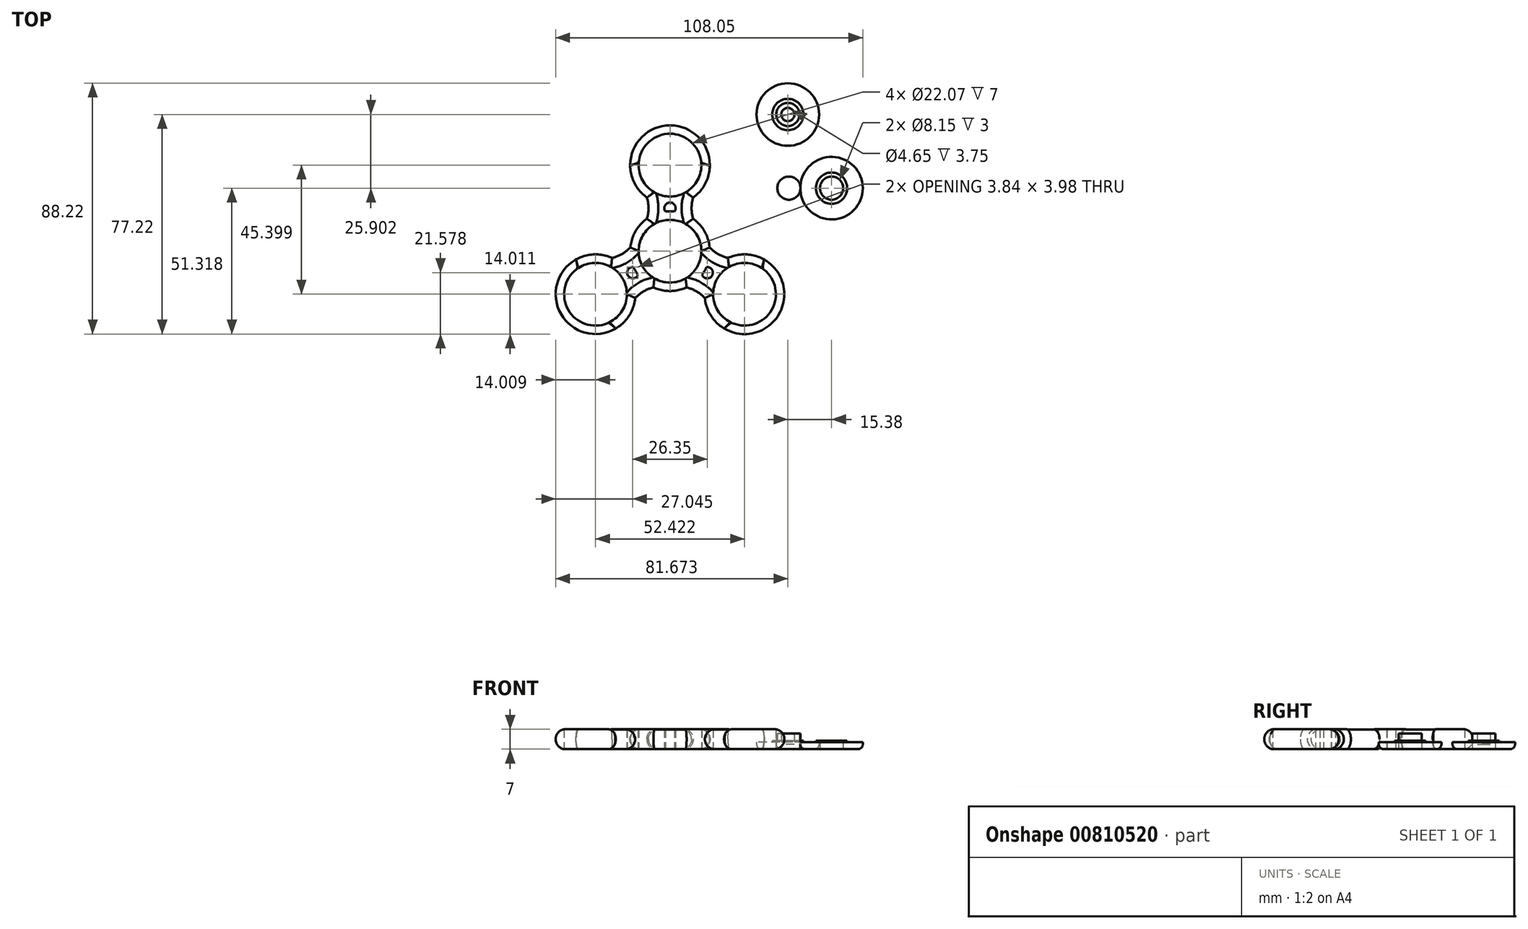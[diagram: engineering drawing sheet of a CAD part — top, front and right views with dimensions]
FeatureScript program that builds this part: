
annotation { "Feature Type Name" : "Feature", "Feature Type Description" : "" }
export const myFeature = defineFeature(function(context is Context, id is Id, definition is map)
    precondition{}
    {
        {
            var Q0;
            Q0=qCreatedBy(makeId("Top.planeOp"),FACE);
            var sketch = newSketch(context, id + "F0", { "sketchPlane" : qUnion([Q0])});
            skLineSegment(sketch, "E0.0", {"start": v(14.14, 16.04) * mm, "end": v(14.14, -14.2) * mm});
            skLineSegment(sketch, "E0.1", {"start": v(14.14, -14.2) * mm, "end": v(-14.14, -14.2) * mm});
            skLineSegment(sketch, "E0.2", {"start": v(-14.14, -14.2) * mm, "end": v(-14.14, 16.08) * mm});
            skLineSegment(sketch, "E0.3", {"start": v(-14.14, 16.08) * mm, "end": v(14.14, 16.04) * mm});
            skPoint(sketch, "E0.0.midPoint", {"position": v(14.14, 0.92) * mm});
            skCircle(sketch, "E1", {"center": v(0, 16.06) * mm, "radius": 14.01 * mm});
            skCircle(sketch, "E2", {"center": v(0, 16.06) * mm, "radius": 11.04 * mm});
            skCircle(sketch, "E3", {"center": v(0, -14.2) * mm, "radius": 14.01 * mm});
            skCircle(sketch, "E4", {"center": v(0, -14.2) * mm, "radius": 11.04 * mm});
            skPoint(sketch, "E5", {"position": v(7.58, 0.92) * mm});
            skPoint(sketch, "E6", {"position": v(-7.58, 0.92) * mm});
            skPoint(sketch, "E7", {"position": v(-14.14, 0.92) * mm});
            skFitSpline(sketch, "E8", {"points": [v(-14.14, 16.08) * mm, v(-7.58, 0.92) * mm, v(-14.14, -14.2) * mm], "startDerivative": vector(19.66, -30.33) * mm, "endDerivative": vector(-19.67, -30.25) * mm});
            skFitSpline(sketch, "E9", {"points": [v(14.14, 16.04) * mm, v(7.58, 0.92) * mm, v(14.14, -14.2) * mm], "startDerivative": vector(-19.67, -30.24) * mm, "endDerivative": vector(19.67, -30.24) * mm});
            skCircle(sketch, "E10", {"center": v(0, 0.92) * mm, "radius": 2 * mm});
            skPoint(sketch, "E11", {"position": v(0, 30.07) * mm});
            skPoint(sketch, "E12", {"position": v(10.48, 25.36) * mm});
            skPoint(sketch, "E13", {"position": v(-10.48, 25.36) * mm});
            skSolve(sketch);
        }
        {
            var Q0;
            Q0=qCreatedBy(makeId("Top.planeOp"),FACE);
            var sketch = newSketch(context, id + "F1", { "sketchPlane" : qUnion([Q0])});
            skCircle(sketch, "E14", {"center": v(41.45, 33.87) * mm, "radius": 11 * mm});
            skCircle(sketch, "E15", {"center": v(41.45, 33.87) * mm, "radius": 5.5 * mm});
            skCircle(sketch, "E16", {"center": v(41.45, 33.87) * mm, "radius": 4.08 * mm});
            skCircle(sketch, "E17", {"center": v(41.83, 7.97) * mm, "radius": 11 * mm});
            skCircle(sketch, "E18", {"center": v(41.83, 7.97) * mm, "radius": 5.5 * mm});
            skCircle(sketch, "E19", {"center": v(41.83, 7.97) * mm, "radius": 4.08 * mm});
            skSolve(sketch);
        }
        {
            var Q0;
            {var subQ1=sQuery(id+"F0.wireOp",EDGE,"E1");var subQ6=sQuery(id+"F0.wireOp",EDGE,"E0.3");var subQ13=makeQuery(id+"F0.imprint","INTERSECT",VERTEX,{"disambiguationData":[OD(0.0)],"derivedFrom":[subQ6,subQ1]});Q0=makeQuery(id+"F0.imprint","IMPRINT",FACE,{"disambiguationData":[TD([[makeQuery(id+"F0.imprint","IMPRINT",EDGE,{"disambiguationData":[TD([[subQ13,-1.0]])],"derivedFrom":subQ6}),1.0]])]});}
            var Q1;
            {var subQ0=sQuery(id+"F0.wireOp",EDGE,"pasm8Eyo-fXrZ-fvG0-8Elu-paJzOGyL3H0m");Q1=makeQuery(id+"F0.imprint","IMPRINT",FACE,{"disambiguationData":[TD([[makeQuery(id+"F0.imprint","IMPRINT",EDGE,{"derivedFrom":subQ0}),1.0]])]});}
            var Q2;
            {var subQ0=sQuery(id+"F0.wireOp",EDGE,"ogIBovJo-0tES-EHRu-C9qO-bWghCShUOrSJ");Q2=makeQuery(id+"F0.imprint","IMPRINT",FACE,{"disambiguationData":[TD([[makeQuery(id+"F0.imprint","IMPRINT",EDGE,{"derivedFrom":subQ0}),1.0]])]});}
            var Q3;
            {var subQ0=sQuery(id+"F0.wireOp",EDGE,"de5ad749-d6f0-4c98-9bd6-3e4d16faad500.MirrorCS");var subQ1=sQuery(id+"F0.wireOp",EDGE,"E1");var subQ2=makeQuery(id+"F0.imprint","INTERSECT",VERTEX,{"disambiguationData":[OD(0.0)],"derivedFrom":[subQ1,subQ0]});Q3=makeQuery(id+"F0.imprint","IMPRINT",FACE,{"disambiguationData":[TD([[makeQuery(id+"F0.imprint","IMPRINT",EDGE,{"disambiguationData":[TD([[subQ2,1.0]])],"derivedFrom":subQ1}),-1.0]])]});}
            var Q4;
            {var subQ0=sQuery(id+"F0.wireOp",EDGE,"005f5cdd-0bdc-4fa0-b84f-56ab7e4a56270.MirrorCS");var subQ3=sQuery(id+"F0.wireOp",EDGE,"E1");var subQ5=makeQuery(id+"F0.imprint","INTERSECT",VERTEX,{"derivedFrom":[subQ3,subQ0]});Q4=makeQuery(id+"F0.imprint","IMPRINT",FACE,{"disambiguationData":[TD([[makeQuery(id+"F0.imprint","IMPRINT",EDGE,{"disambiguationData":[TD([[subQ5,1.0]])],"derivedFrom":subQ3}),-1.0]])]});}
            var Q5;
            {var subQ0=sQuery(id+"F0.wireOp",EDGE,"E9");var subQ1=sQuery(id+"F0.wireOp",EDGE,"E1");var subQ2=makeQuery(id+"F0.imprint","INTERSECT",VERTEX,{"disambiguationData":[OD(0.0)],"derivedFrom":[subQ1,subQ0]});Q5=makeQuery(id+"F0.imprint","IMPRINT",FACE,{"disambiguationData":[TD([[makeQuery(id+"F0.imprint","IMPRINT",EDGE,{"disambiguationData":[TD([[subQ2,-1.0]])],"derivedFrom":subQ1}),1.0]])]});}
            var Q6;
            {var subQ1=sQuery(id+"F0.wireOp",EDGE,"E1");var subQ5=sQuery(id+"F0.wireOp",EDGE,"E0.3");var subQ6=makeQuery(id+"F0.imprint","INTERSECT",VERTEX,{"disambiguationData":[OD(0.0)],"derivedFrom":[subQ5,subQ1]});Q6=makeQuery(id+"F0.imprint","IMPRINT",FACE,{"disambiguationData":[TD([[makeQuery(id+"F0.imprint","IMPRINT",EDGE,{"disambiguationData":[TD([[subQ6,-1.0]])],"derivedFrom":subQ5}),-1.0]])]});}
            var Q7;
            {var subQ0=sQuery(id+"F0.wireOp",EDGE,"E8");var subQ1=sQuery(id+"F0.wireOp",EDGE,"E1");var subQ2=makeQuery(id+"F0.imprint","INTERSECT",VERTEX,{"disambiguationData":[OD(0.0)],"derivedFrom":[subQ1,subQ0]});Q7=makeQuery(id+"F0.imprint","IMPRINT",FACE,{"disambiguationData":[TD([[makeQuery(id+"F0.imprint","IMPRINT",EDGE,{"disambiguationData":[TD([[subQ2,-1.0]])],"derivedFrom":subQ1}),1.0]])]});}
            var Q8;
            {var subQ0=sQuery(id+"F0.wireOp",EDGE,"E8");var subQ1=sQuery(id+"F0.wireOp",EDGE,"E1");var subQ2=makeQuery(id+"F0.imprint","INTERSECT",VERTEX,{"disambiguationData":[OD(1.0)],"derivedFrom":[subQ1,subQ0]});Q8=makeQuery(id+"F0.imprint","IMPRINT",FACE,{"disambiguationData":[TD([[makeQuery(id+"F0.imprint","IMPRINT",EDGE,{"disambiguationData":[TD([[subQ2,-1.0]])],"derivedFrom":subQ1}),-1.0]])]});}
            var Q9;
            {var subQ0=sQuery(id+"F0.wireOp",EDGE,"E10");var subQ1=sQuery(id+"F0.wireOp",EDGE,"E1");var subQ2=makeQuery(id+"F0.imprint","INTERSECT",VERTEX,{"disambiguationData":[OD(1.0)],"derivedFrom":[subQ1,subQ0]});Q9=makeQuery(id+"F0.imprint","IMPRINT",FACE,{"disambiguationData":[TD([[makeQuery(id+"F0.imprint","IMPRINT",EDGE,{"disambiguationData":[TD([[subQ2,-1.0]])],"derivedFrom":subQ1}),-1.0]])]});}
            var Q10;
            {var subQ0=sQuery(id+"F0.wireOp",EDGE,"E8");var subQ1=sQuery(id+"F0.wireOp",EDGE,"E3");var subQ2=makeQuery(id+"F0.imprint","INTERSECT",VERTEX,{"disambiguationData":[OD(0.0)],"derivedFrom":[subQ1,subQ0]});Q10=makeQuery(id+"F0.imprint","IMPRINT",FACE,{"disambiguationData":[TD([[makeQuery(id+"F0.imprint","IMPRINT",EDGE,{"disambiguationData":[TD([[subQ2,-1.0]])],"derivedFrom":subQ1}),1.0]])]});}
            var Q11;
            {var subQ0=sQuery(id+"F0.wireOp",EDGE,"E9");var subQ1=sQuery(id+"F0.wireOp",EDGE,"E3");var subQ2=makeQuery(id+"F0.imprint","INTERSECT",VERTEX,{"disambiguationData":[OD(0.0)],"derivedFrom":[subQ1,subQ0]});Q11=makeQuery(id+"F0.imprint","IMPRINT",FACE,{"disambiguationData":[TD([[makeQuery(id+"F0.imprint","IMPRINT",EDGE,{"disambiguationData":[TD([[subQ2,-1.0]])],"derivedFrom":subQ1}),1.0]])]});}
            var Q12;
            {var subQ0=sQuery(id+"F0.wireOp",EDGE,"E3");var subQ1=sQuery(id+"F0.wireOp",EDGE,"E0.1");var subQ2=makeQuery(id+"F0.imprint","INTERSECT",VERTEX,{"disambiguationData":[OD(0.0)],"derivedFrom":[subQ1,subQ0]});Q12=makeQuery(id+"F0.imprint","IMPRINT",FACE,{"disambiguationData":[TD([[makeQuery(id+"F0.imprint","IMPRINT",EDGE,{"disambiguationData":[TD([[subQ2,-1.0]])],"derivedFrom":subQ1}),1.0]])]});}
            var Q13;
            {var subQ1=sQuery(id+"F0.wireOp",EDGE,"E3");var subQ5=sQuery(id+"F0.wireOp",EDGE,"E0.1");var subQ6=makeQuery(id+"F0.imprint","INTERSECT",VERTEX,{"disambiguationData":[OD(0.0)],"derivedFrom":[subQ5,subQ1]});Q13=makeQuery(id+"F0.imprint","IMPRINT",FACE,{"disambiguationData":[TD([[makeQuery(id+"F0.imprint","IMPRINT",EDGE,{"disambiguationData":[TD([[subQ6,-1.0]])],"derivedFrom":subQ5}),-1.0]])]});}
            extrude(context, id + "F2", {"entities" : qUnion([Q0, Q1, Q2, Q3, Q4, Q5, Q6, Q7, Q8, Q9, Q10, Q11, Q12, Q13]), "depth" : 7 * mm, "offsetDistance" : 25 * mm});
        }
        {
            var Q0;
            Q0=makeQuery(id+"F2.opExtrude","SWEPT_BODY",BODY,{"disambiguationData":[OSD([sQuery(id+"F0.wireOp",EDGE,"E0.0"),sQuery(id+"F0.wireOp",EDGE,"E0.1"),sQuery(id+"F0.wireOp",EDGE,"E0.2"),sQuery(id+"F0.wireOp",EDGE,"E0.3"),sQuery(id+"F0.wireOp",EDGE,"E1"),sQuery(id+"F0.wireOp",EDGE,"E2"),sQuery(id+"F0.wireOp",EDGE,"E3"),sQuery(id+"F0.wireOp",EDGE,"E4")])]});
            var Q1;
            Q1=sQuery(id+"F0.wireOp",EDGE,"E4");
            circularPattern(context, id + "F3", {"entities" : qUnion([Q0]), "axis" : qUnion([Q1]), "angle" : 360 * degree, "instanceCount" : 3, "equalSpace" : true});
        }
        {
            var Q0;
            Q0=makeQuery(id+"F2.opExtrude","SWEPT_BODY",BODY,{"disambiguationData":[OSD([sQuery(id+"F0.wireOp",EDGE,"E0.0"),sQuery(id+"F0.wireOp",EDGE,"E0.1"),sQuery(id+"F0.wireOp",EDGE,"E0.2"),sQuery(id+"F0.wireOp",EDGE,"E0.3"),sQuery(id+"F0.wireOp",EDGE,"E1"),sQuery(id+"F0.wireOp",EDGE,"E2"),sQuery(id+"F0.wireOp",EDGE,"E3"),sQuery(id+"F0.wireOp",EDGE,"E4")])]});
            var Q1;
            Q1=makeQuery(id+"F3.opPattern","COPY",BODY,{"derivedFrom":makeQuery(id+"F2.opExtrude","SWEPT_BODY",BODY,{"disambiguationData":[OSD([sQuery(id+"F0.wireOp",EDGE,"E0.0"),sQuery(id+"F0.wireOp",EDGE,"E0.1"),sQuery(id+"F0.wireOp",EDGE,"E0.2"),sQuery(id+"F0.wireOp",EDGE,"E0.3"),sQuery(id+"F0.wireOp",EDGE,"E1"),sQuery(id+"F0.wireOp",EDGE,"E2"),sQuery(id+"F0.wireOp",EDGE,"E3"),sQuery(id+"F0.wireOp",EDGE,"E4")])]}),"instanceName":"3"});
            var Q2;
            Q2=makeQuery(id+"F3.opPattern","COPY",BODY,{"derivedFrom":makeQuery(id+"F2.opExtrude","SWEPT_BODY",BODY,{"disambiguationData":[OSD([sQuery(id+"F0.wireOp",EDGE,"E0.0"),sQuery(id+"F0.wireOp",EDGE,"E0.1"),sQuery(id+"F0.wireOp",EDGE,"E0.2"),sQuery(id+"F0.wireOp",EDGE,"E0.3"),sQuery(id+"F0.wireOp",EDGE,"E1"),sQuery(id+"F0.wireOp",EDGE,"E2"),sQuery(id+"F0.wireOp",EDGE,"E3"),sQuery(id+"F0.wireOp",EDGE,"E4")])]}),"instanceName":"4"});
            var Q3;
            Q3=makeQuery(id+"F3.opPattern","COPY",BODY,{"derivedFrom":makeQuery(id+"F2.opExtrude","SWEPT_BODY",BODY,{"disambiguationData":[OSD([sQuery(id+"F0.wireOp",EDGE,"E0.0"),sQuery(id+"F0.wireOp",EDGE,"E0.1"),sQuery(id+"F0.wireOp",EDGE,"E0.2"),sQuery(id+"F0.wireOp",EDGE,"E0.3"),sQuery(id+"F0.wireOp",EDGE,"E1"),sQuery(id+"F0.wireOp",EDGE,"E2"),sQuery(id+"F0.wireOp",EDGE,"E3"),sQuery(id+"F0.wireOp",EDGE,"E4")])]}),"instanceName":"1"});
            var Q4;
            Q4=makeQuery(id+"F3.opPattern","COPY",BODY,{"derivedFrom":makeQuery(id+"F2.opExtrude","SWEPT_BODY",BODY,{"disambiguationData":[OSD([sQuery(id+"F0.wireOp",EDGE,"E0.0"),sQuery(id+"F0.wireOp",EDGE,"E0.1"),sQuery(id+"F0.wireOp",EDGE,"E0.2"),sQuery(id+"F0.wireOp",EDGE,"E0.3"),sQuery(id+"F0.wireOp",EDGE,"E1"),sQuery(id+"F0.wireOp",EDGE,"E2"),sQuery(id+"F0.wireOp",EDGE,"E3"),sQuery(id+"F0.wireOp",EDGE,"E4")])]}),"instanceName":"2"});
            var Q5;
            Q5=makeQuery(id+"F3.opPattern","COPY",BODY,{"derivedFrom":makeQuery(id+"F2.opExtrude","SWEPT_BODY",BODY,{"disambiguationData":[OSD([sQuery(id+"F0.wireOp",EDGE,"E0.0"),sQuery(id+"F0.wireOp",EDGE,"E0.1"),sQuery(id+"F0.wireOp",EDGE,"E0.2"),sQuery(id+"F0.wireOp",EDGE,"E0.3"),sQuery(id+"F0.wireOp",EDGE,"E1"),sQuery(id+"F0.wireOp",EDGE,"E2"),sQuery(id+"F0.wireOp",EDGE,"E3"),sQuery(id+"F0.wireOp",EDGE,"E4")])]}),"instanceName":"5"});
            booleanBodies(context, id + "F4", {"operationType" : BooleanOperationType.UNION, "tools" : qUnion([Q0, Q1, Q2, Q3, Q4, Q5])});
        }
        {
            var Q0;
            Q0=makeQuery(id+"F1.imprint","IMPRINT",FACE,{"disambiguationData":[TD([[makeQuery(id+"F1.imprint","IMPRINT",EDGE,{"derivedFrom":sQuery(id+"F1.wireOp",EDGE,"E14")}),1.0]])]});
            var Q1;
            Q1=makeQuery(id+"F1.imprint","IMPRINT",FACE,{"disambiguationData":[TD([[makeQuery(id+"F1.imprint","IMPRINT",EDGE,{"derivedFrom":sQuery(id+"F1.wireOp",EDGE,"E17")}),1.0]])]});
            extrude(context, id + "F5", {"entities" : qUnion([Q0, Q1]), "depth" : 2.5 * mm, "offsetDistance" : 25 * mm});
        }
        {
            var Q0;
            Q0=makeQuery(id+"F1.imprint","IMPRINT",FACE,{"disambiguationData":[TD([[makeQuery(id+"F1.imprint","IMPRINT",EDGE,{"derivedFrom":sQuery(id+"F1.wireOp",EDGE,"E15")}),1.0]])]});
            extrude(context, id + "F6", {"entities" : qUnion([Q0]), "operationType" : NewBodyOperationType.ADD, "depth" : 3 * mm, "offsetDistance" : 25 * mm});
        }
        {
            var Q0;
            Q0=makeQuery(id+"F1.imprint","IMPRINT",FACE,{"disambiguationData":[TD([[makeQuery(id+"F1.imprint","IMPRINT",EDGE,{"derivedFrom":sQuery(id+"F1.wireOp",EDGE,"E18")}),1.0]])]});
            extrude(context, id + "F7", {"entities" : qUnion([Q0]), "operationType" : NewBodyOperationType.ADD, "depth" : 3 * mm, "offsetDistance" : 25 * mm});
        }
        {
            var Q0;
            Q0=makeQuery(id+"F1.imprint","IMPRINT",FACE,{"disambiguationData":[TD([[makeQuery(id+"F1.imprint","IMPRINT",EDGE,{"derivedFrom":sQuery(id+"F1.wireOp",EDGE,"E19")}),1.0]])]});
            var Q1;
            Q1=makeQuery(id+"F1.imprint","IMPRINT",FACE,{"disambiguationData":[TD([[makeQuery(id+"F1.imprint","IMPRINT",EDGE,{"derivedFrom":sQuery(id+"F1.wireOp",EDGE,"E16")}),1.0]])]});
            extrude(context, id + "F8", {"entities" : qUnion([Q0, Q1]), "depth" : 5.5 * mm, "offsetDistance" : 25 * mm});
        }
        {
            var Q0;
            Q0=makeQuery(id+"F5.opExtrude","CAP_EDGE",EDGE,{"disambiguationData":[OSD([sQuery(id+"F1.wireOp",EDGE,"E14")])],"isStart":true});
            var Q1;
            Q1=makeQuery(id+"F5.opExtrude","CAP_EDGE",EDGE,{"disambiguationData":[OSD([sQuery(id+"F1.wireOp",EDGE,"E17")])],"isStart":true});
            fillet(context, id + "F9", {"entities" : qUnion([Q0, Q1]), "radius" : 1.75 * mm, "tangentPropagation" : true, "allowEdgeOverflow" : false});
        }
        {
            var Q0;
            Q0=makeQuery(id+"F5.opExtrude","SWEPT_BODY",BODY,{"disambiguationData":[OSD([sQuery(id+"F1.wireOp",EDGE,"E17"),sQuery(id+"F1.wireOp",EDGE,"E18")])]});
            transform(context, id + "F10", {"entities" : qUnion([Q0]), "transformType" : TransformType.TRANSLATION_3D, "dx" : 15 * mm, "dy" : 0 * mm, "dz" : 0 * mm, "makeCopy" : true});
        }
        {
            var Q0;
            Q0=makeQuery(id+"F5.opExtrude","SWEPT_BODY",BODY,{"disambiguationData":[OSD([sQuery(id+"F1.wireOp",EDGE,"E17"),sQuery(id+"F1.wireOp",EDGE,"E18")])]});
            deleteBodies(context, id + "F11", {"entities" : qUnion([Q0])});
        }
        {
            var Q0;
            {var subQ0=sQuery(id+"F0.wireOp",EDGE,"E1");var subQ1=sQuery(id+"F0.wireOp",EDGE,"E9");Q0=makeQuery(id+"F3.opPattern","COPY",EDGE,{"derivedFrom":makeQuery(id+"F2.opExtrude","CAP_EDGE",EDGE,{"disambiguationData":[OSD([subQ0]),TDD([makeQuery(id+"F0.imprint","IMPRINT",EDGE,{"disambiguationData":[TD([[makeQuery(id+"F0.imprint","INTERSECT",VERTEX,{"disambiguationData":[OD(0.0)],"derivedFrom":[subQ0,subQ1]}),-1.0]])],"derivedFrom":subQ0}),makeQuery(id+"F0.imprint","IMPRINT",EDGE,{"disambiguationData":[TD([[makeQuery(id+"F0.imprint","INTERSECT",VERTEX,{"disambiguationData":[OD(1.0)],"derivedFrom":[sQuery(id+"F0.wireOp",EDGE,"E0.3"),subQ0]}),1.0]])],"derivedFrom":subQ0})])],"isStart":false}),"instanceName":"1"});}
            var Q1;
            Q1=makeQuery(id+"F3.opPattern","COPY",EDGE,{"derivedFrom":makeQuery(id+"F2.opExtrude","CAP_EDGE",EDGE,{"disambiguationData":[OSD([sQuery(id+"F0.wireOp",EDGE,"005f5cdd-0bdc-4fa0-b84f-56ab7e4a56270.MirrorCS")])],"isStart":false}),"instanceName":"1"});
            var Q2;
            Q2=makeQuery(id+"F3.opPattern","COPY",EDGE,{"derivedFrom":makeQuery(id+"F2.opExtrude","CAP_EDGE",EDGE,{"disambiguationData":[OSD([sQuery(id+"F0.wireOp",EDGE,"de5ad749-d6f0-4c98-9bd6-3e4d16faad500.MirrorCS")])],"isStart":false}),"instanceName":"1"});
            var Q3;
            Q3=makeQuery(id+"F3.opPattern","COPY",EDGE,{"derivedFrom":makeQuery(id+"F2.opExtrude","CAP_EDGE",EDGE,{"disambiguationData":[OSD([sQuery(id+"F0.wireOp",EDGE,"ogIBovJo-0tES-EHRu-C9qO-bWghCShUOrSJ")])],"isStart":false}),"instanceName":"1"});
            var Q4;
            Q4=makeQuery(id+"F3.opPattern","COPY",EDGE,{"derivedFrom":makeQuery(id+"F2.opExtrude","CAP_EDGE",EDGE,{"disambiguationData":[OSD([sQuery(id+"F0.wireOp",EDGE,"pasm8Eyo-fXrZ-fvG0-8Elu-paJzOGyL3H0m")])],"isStart":false}),"instanceName":"1"});
            var Q5;
            {var subQ0=sQuery(id+"F0.wireOp",EDGE,"E8");var subQ1=sQuery(id+"F0.wireOp",EDGE,"E1");var subQ2=makeQuery(id+"F0.imprint","INTERSECT",VERTEX,{"disambiguationData":[OD(0.0)],"derivedFrom":[subQ1,subQ0]});Q5=makeQuery(id+"F3.opPattern","COPY",EDGE,{"derivedFrom":makeQuery(id+"F2.opExtrude","CAP_EDGE",EDGE,{"disambiguationData":[OSD([subQ1]),TDD([makeQuery(id+"F0.imprint","IMPRINT",EDGE,{"disambiguationData":[TD([[makeQuery(id+"F0.imprint","INTERSECT",VERTEX,{"disambiguationData":[OD(0.0)],"derivedFrom":[sQuery(id+"F0.wireOp",EDGE,"E0.3"),subQ1]}),-1.0]])],"derivedFrom":subQ1}),makeQuery(id+"F0.imprint","IMPRINT",EDGE,{"disambiguationData":[TD([[subQ2,-1.0]])],"derivedFrom":subQ1})])],"isStart":false}),"instanceName":"1"});}
            var Q6;
            Q6=makeQuery(id+"F3.opPattern","COPY",EDGE,{"derivedFrom":makeQuery(id+"F2.opExtrude","CAP_EDGE",EDGE,{"disambiguationData":[OSD([sQuery(id+"F0.wireOp",EDGE,"E8")])],"isStart":false}),"instanceName":"1"});
            var Q7;
            Q7=makeQuery(id+"F3.opPattern","COPY",EDGE,{"derivedFrom":makeQuery(id+"F2.opExtrude","CAP_EDGE",EDGE,{"disambiguationData":[OSD([sQuery(id+"F0.wireOp",EDGE,"E9")])],"isStart":false}),"instanceName":"1"});
            var Q8;
            {var subQ0=sQuery(id+"F0.wireOp",EDGE,"E8");var subQ2=sQuery(id+"F0.wireOp",EDGE,"E3");Q8=makeQuery(id+"F4.opBoolean","SPLIT",EDGE,{"disambiguationData":[TD([makeQuery(id+"F2.opExtrude","SWEPT_FACE",FACE,{"disambiguationData":[OSD([subQ0])]})])],"derivedFrom":makeQuery(id+"F2.opExtrude","CAP_EDGE",EDGE,{"disambiguationData":[OSD([subQ2])],"isStart":false})});}
            var Q9;
            {var subQ0=sQuery(id+"F0.wireOp",EDGE,"E8");var subQ2=sQuery(id+"F0.wireOp",EDGE,"E3");Q9=makeQuery(id+"F4.opBoolean","SPLIT",EDGE,{"disambiguationData":[TD([makeQuery(id+"F3.opPattern","COPY",FACE,{"derivedFrom":makeQuery(id+"F2.opExtrude","SWEPT_FACE",FACE,{"disambiguationData":[OSD([subQ0])]}),"instanceName":"1"})])],"derivedFrom":makeQuery(id+"F2.opExtrude","CAP_EDGE",EDGE,{"disambiguationData":[OSD([subQ2])],"isStart":false})});}
            var Q10;
            Q10=makeQuery(id+"F3.opPattern","COPY",EDGE,{"derivedFrom":makeQuery(id+"F2.opExtrude","CAP_EDGE",EDGE,{"disambiguationData":[OSD([sQuery(id+"F0.wireOp",EDGE,"E9")])],"isStart":false}),"instanceName":"2"});
            var Q11;
            {var subQ0=sQuery(id+"F0.wireOp",EDGE,"E9");var subQ2=sQuery(id+"F0.wireOp",EDGE,"E3");Q11=makeQuery(id+"F4.opBoolean","SPLIT",EDGE,{"disambiguationData":[TD([makeQuery(id+"F2.opExtrude","SWEPT_FACE",FACE,{"disambiguationData":[OSD([subQ0])]})])],"derivedFrom":makeQuery(id+"F2.opExtrude","CAP_EDGE",EDGE,{"disambiguationData":[OSD([subQ2])],"isStart":false})});}
            var Q12;
            Q12=makeQuery(id+"F2.opExtrude","CAP_EDGE",EDGE,{"disambiguationData":[OSD([sQuery(id+"F0.wireOp",EDGE,"E9")])],"isStart":false});
            var Q13;
            Q13=makeQuery(id+"F2.opExtrude","CAP_EDGE",EDGE,{"disambiguationData":[OSD([sQuery(id+"F0.wireOp",EDGE,"E8")])],"isStart":false});
            var Q14;
            {var subQ0=sQuery(id+"F0.wireOp",EDGE,"E8");var subQ1=sQuery(id+"F0.wireOp",EDGE,"E1");var subQ2=makeQuery(id+"F0.imprint","INTERSECT",VERTEX,{"disambiguationData":[OD(0.0)],"derivedFrom":[subQ1,subQ0]});Q14=makeQuery(id+"F2.opExtrude","CAP_EDGE",EDGE,{"disambiguationData":[OSD([subQ1]),TDD([makeQuery(id+"F0.imprint","IMPRINT",EDGE,{"disambiguationData":[TD([[makeQuery(id+"F0.imprint","INTERSECT",VERTEX,{"disambiguationData":[OD(0.0)],"derivedFrom":[sQuery(id+"F0.wireOp",EDGE,"E0.3"),subQ1]}),-1.0]])],"derivedFrom":subQ1}),makeQuery(id+"F0.imprint","IMPRINT",EDGE,{"disambiguationData":[TD([[subQ2,-1.0]])],"derivedFrom":subQ1})])],"isStart":false});}
            var Q15;
            Q15=makeQuery(id+"F2.opExtrude","CAP_EDGE",EDGE,{"disambiguationData":[OSD([sQuery(id+"F0.wireOp",EDGE,"pasm8Eyo-fXrZ-fvG0-8Elu-paJzOGyL3H0m")])],"isStart":false});
            var Q16;
            Q16=makeQuery(id+"F2.opExtrude","CAP_EDGE",EDGE,{"disambiguationData":[OSD([sQuery(id+"F0.wireOp",EDGE,"ogIBovJo-0tES-EHRu-C9qO-bWghCShUOrSJ")])],"isStart":false});
            var Q17;
            Q17=makeQuery(id+"F2.opExtrude","CAP_EDGE",EDGE,{"disambiguationData":[OSD([sQuery(id+"F0.wireOp",EDGE,"de5ad749-d6f0-4c98-9bd6-3e4d16faad500.MirrorCS")])],"isStart":false});
            var Q18;
            Q18=makeQuery(id+"F2.opExtrude","CAP_EDGE",EDGE,{"disambiguationData":[OSD([sQuery(id+"F0.wireOp",EDGE,"005f5cdd-0bdc-4fa0-b84f-56ab7e4a56270.MirrorCS")])],"isStart":false});
            var Q19;
            {var subQ0=sQuery(id+"F0.wireOp",EDGE,"E1");var subQ1=sQuery(id+"F0.wireOp",EDGE,"E9");Q19=makeQuery(id+"F2.opExtrude","CAP_EDGE",EDGE,{"disambiguationData":[OSD([subQ0]),TDD([makeQuery(id+"F0.imprint","IMPRINT",EDGE,{"disambiguationData":[TD([[makeQuery(id+"F0.imprint","INTERSECT",VERTEX,{"disambiguationData":[OD(0.0)],"derivedFrom":[subQ0,subQ1]}),-1.0]])],"derivedFrom":subQ0}),makeQuery(id+"F0.imprint","IMPRINT",EDGE,{"disambiguationData":[TD([[makeQuery(id+"F0.imprint","INTERSECT",VERTEX,{"disambiguationData":[OD(1.0)],"derivedFrom":[sQuery(id+"F0.wireOp",EDGE,"E0.3"),subQ0]}),1.0]])],"derivedFrom":subQ0})])],"isStart":false});}
            var Q20;
            Q20=makeQuery(id+"F3.opPattern","COPY",EDGE,{"derivedFrom":makeQuery(id+"F2.opExtrude","CAP_EDGE",EDGE,{"disambiguationData":[OSD([sQuery(id+"F0.wireOp",EDGE,"E8")])],"isStart":false}),"instanceName":"2"});
            var Q21;
            {var subQ0=sQuery(id+"F0.wireOp",EDGE,"E8");var subQ1=sQuery(id+"F0.wireOp",EDGE,"E1");var subQ2=makeQuery(id+"F0.imprint","INTERSECT",VERTEX,{"disambiguationData":[OD(0.0)],"derivedFrom":[subQ1,subQ0]});Q21=makeQuery(id+"F3.opPattern","COPY",EDGE,{"derivedFrom":makeQuery(id+"F2.opExtrude","CAP_EDGE",EDGE,{"disambiguationData":[OSD([subQ1]),TDD([makeQuery(id+"F0.imprint","IMPRINT",EDGE,{"disambiguationData":[TD([[makeQuery(id+"F0.imprint","INTERSECT",VERTEX,{"disambiguationData":[OD(0.0)],"derivedFrom":[sQuery(id+"F0.wireOp",EDGE,"E0.3"),subQ1]}),-1.0]])],"derivedFrom":subQ1}),makeQuery(id+"F0.imprint","IMPRINT",EDGE,{"disambiguationData":[TD([[subQ2,-1.0]])],"derivedFrom":subQ1})])],"isStart":false}),"instanceName":"2"});}
            var Q22;
            Q22=makeQuery(id+"F3.opPattern","COPY",EDGE,{"derivedFrom":makeQuery(id+"F2.opExtrude","CAP_EDGE",EDGE,{"disambiguationData":[OSD([sQuery(id+"F0.wireOp",EDGE,"pasm8Eyo-fXrZ-fvG0-8Elu-paJzOGyL3H0m")])],"isStart":false}),"instanceName":"2"});
            var Q23;
            Q23=makeQuery(id+"F3.opPattern","COPY",EDGE,{"derivedFrom":makeQuery(id+"F2.opExtrude","CAP_EDGE",EDGE,{"disambiguationData":[OSD([sQuery(id+"F0.wireOp",EDGE,"ogIBovJo-0tES-EHRu-C9qO-bWghCShUOrSJ")])],"isStart":false}),"instanceName":"2"});
            var Q24;
            {var subQ0=sQuery(id+"F0.wireOp",EDGE,"E1");var subQ1=sQuery(id+"F0.wireOp",EDGE,"E9");Q24=makeQuery(id+"F3.opPattern","COPY",EDGE,{"derivedFrom":makeQuery(id+"F2.opExtrude","CAP_EDGE",EDGE,{"disambiguationData":[OSD([subQ0]),TDD([makeQuery(id+"F0.imprint","IMPRINT",EDGE,{"disambiguationData":[TD([[makeQuery(id+"F0.imprint","INTERSECT",VERTEX,{"disambiguationData":[OD(0.0)],"derivedFrom":[subQ0,subQ1]}),-1.0]])],"derivedFrom":subQ0}),makeQuery(id+"F0.imprint","IMPRINT",EDGE,{"disambiguationData":[TD([[makeQuery(id+"F0.imprint","INTERSECT",VERTEX,{"disambiguationData":[OD(1.0)],"derivedFrom":[sQuery(id+"F0.wireOp",EDGE,"E0.3"),subQ0]}),1.0]])],"derivedFrom":subQ0})])],"isStart":false}),"instanceName":"2"});}
            var Q25;
            Q25=makeQuery(id+"F3.opPattern","COPY",EDGE,{"derivedFrom":makeQuery(id+"F2.opExtrude","CAP_EDGE",EDGE,{"disambiguationData":[OSD([sQuery(id+"F0.wireOp",EDGE,"005f5cdd-0bdc-4fa0-b84f-56ab7e4a56270.MirrorCS")])],"isStart":false}),"instanceName":"2"});
            var Q26;
            Q26=makeQuery(id+"F3.opPattern","COPY",EDGE,{"derivedFrom":makeQuery(id+"F2.opExtrude","CAP_EDGE",EDGE,{"disambiguationData":[OSD([sQuery(id+"F0.wireOp",EDGE,"de5ad749-d6f0-4c98-9bd6-3e4d16faad500.MirrorCS")])],"isStart":false}),"instanceName":"2"});
            var Q27;
            {var subQ0=sQuery(id+"F0.wireOp",EDGE,"E9");var subQ2=sQuery(id+"F0.wireOp",EDGE,"E3");Q27=makeQuery(id+"F4.opBoolean","SPLIT",EDGE,{"disambiguationData":[TD([makeQuery(id+"F2.opExtrude","SWEPT_FACE",FACE,{"disambiguationData":[OSD([subQ0])]})])],"derivedFrom":makeQuery(id+"F2.opExtrude","CAP_EDGE",EDGE,{"disambiguationData":[OSD([subQ2])],"isStart":true})});}
            var Q28;
            Q28=makeQuery(id+"F2.opExtrude","CAP_EDGE",EDGE,{"disambiguationData":[OSD([sQuery(id+"F0.wireOp",EDGE,"E9")])],"isStart":true});
            var Q29;
            {var subQ0=sQuery(id+"F0.wireOp",EDGE,"E1");var subQ1=sQuery(id+"F0.wireOp",EDGE,"E9");Q29=makeQuery(id+"F2.opExtrude","CAP_EDGE",EDGE,{"disambiguationData":[OSD([subQ0]),TDD([makeQuery(id+"F0.imprint","IMPRINT",EDGE,{"disambiguationData":[TD([[makeQuery(id+"F0.imprint","INTERSECT",VERTEX,{"disambiguationData":[OD(0.0)],"derivedFrom":[subQ0,subQ1]}),-1.0]])],"derivedFrom":subQ0}),makeQuery(id+"F0.imprint","IMPRINT",EDGE,{"disambiguationData":[TD([[makeQuery(id+"F0.imprint","INTERSECT",VERTEX,{"disambiguationData":[OD(1.0)],"derivedFrom":[sQuery(id+"F0.wireOp",EDGE,"E0.3"),subQ0]}),1.0]])],"derivedFrom":subQ0})])],"isStart":true});}
            var Q30;
            Q30=makeQuery(id+"F2.opExtrude","CAP_EDGE",EDGE,{"disambiguationData":[OSD([sQuery(id+"F0.wireOp",EDGE,"005f5cdd-0bdc-4fa0-b84f-56ab7e4a56270.MirrorCS")])],"isStart":true});
            var Q31;
            Q31=makeQuery(id+"F2.opExtrude","CAP_EDGE",EDGE,{"disambiguationData":[OSD([sQuery(id+"F0.wireOp",EDGE,"de5ad749-d6f0-4c98-9bd6-3e4d16faad500.MirrorCS")])],"isStart":true});
            var Q32;
            Q32=makeQuery(id+"F2.opExtrude","CAP_EDGE",EDGE,{"disambiguationData":[OSD([sQuery(id+"F0.wireOp",EDGE,"ogIBovJo-0tES-EHRu-C9qO-bWghCShUOrSJ")])],"isStart":true});
            var Q33;
            Q33=makeQuery(id+"F2.opExtrude","CAP_EDGE",EDGE,{"disambiguationData":[OSD([sQuery(id+"F0.wireOp",EDGE,"pasm8Eyo-fXrZ-fvG0-8Elu-paJzOGyL3H0m")])],"isStart":true});
            var Q34;
            {var subQ0=sQuery(id+"F0.wireOp",EDGE,"E8");var subQ1=sQuery(id+"F0.wireOp",EDGE,"E1");var subQ2=makeQuery(id+"F0.imprint","INTERSECT",VERTEX,{"disambiguationData":[OD(0.0)],"derivedFrom":[subQ1,subQ0]});Q34=makeQuery(id+"F2.opExtrude","CAP_EDGE",EDGE,{"disambiguationData":[OSD([subQ1]),TDD([makeQuery(id+"F0.imprint","IMPRINT",EDGE,{"disambiguationData":[TD([[makeQuery(id+"F0.imprint","INTERSECT",VERTEX,{"disambiguationData":[OD(0.0)],"derivedFrom":[sQuery(id+"F0.wireOp",EDGE,"E0.3"),subQ1]}),-1.0]])],"derivedFrom":subQ1}),makeQuery(id+"F0.imprint","IMPRINT",EDGE,{"disambiguationData":[TD([[subQ2,-1.0]])],"derivedFrom":subQ1})])],"isStart":true});}
            var Q35;
            Q35=makeQuery(id+"F2.opExtrude","CAP_EDGE",EDGE,{"disambiguationData":[OSD([sQuery(id+"F0.wireOp",EDGE,"E8")])],"isStart":true});
            var Q36;
            {var subQ1=sQuery(id+"F0.wireOp",EDGE,"E8");var subQ2=sQuery(id+"F0.wireOp",EDGE,"E3");Q36=makeQuery(id+"F4.opBoolean","SPLIT",EDGE,{"disambiguationData":[TD([makeQuery(id+"F2.opExtrude","SWEPT_FACE",FACE,{"disambiguationData":[OSD([subQ1])]})])],"derivedFrom":makeQuery(id+"F2.opExtrude","CAP_EDGE",EDGE,{"disambiguationData":[OSD([subQ2])],"isStart":true})});}
            var Q37;
            Q37=makeQuery(id+"F3.opPattern","COPY",EDGE,{"derivedFrom":makeQuery(id+"F2.opExtrude","CAP_EDGE",EDGE,{"disambiguationData":[OSD([sQuery(id+"F0.wireOp",EDGE,"E9")])],"isStart":true}),"instanceName":"1"});
            var Q38;
            {var subQ0=sQuery(id+"F0.wireOp",EDGE,"E1");var subQ1=sQuery(id+"F0.wireOp",EDGE,"E9");Q38=makeQuery(id+"F3.opPattern","COPY",EDGE,{"derivedFrom":makeQuery(id+"F2.opExtrude","CAP_EDGE",EDGE,{"disambiguationData":[OSD([subQ0]),TDD([makeQuery(id+"F0.imprint","IMPRINT",EDGE,{"disambiguationData":[TD([[makeQuery(id+"F0.imprint","INTERSECT",VERTEX,{"disambiguationData":[OD(0.0)],"derivedFrom":[subQ0,subQ1]}),-1.0]])],"derivedFrom":subQ0}),makeQuery(id+"F0.imprint","IMPRINT",EDGE,{"disambiguationData":[TD([[makeQuery(id+"F0.imprint","INTERSECT",VERTEX,{"disambiguationData":[OD(1.0)],"derivedFrom":[sQuery(id+"F0.wireOp",EDGE,"E0.3"),subQ0]}),1.0]])],"derivedFrom":subQ0})])],"isStart":true}),"instanceName":"1"});}
            var Q39;
            Q39=makeQuery(id+"F3.opPattern","COPY",EDGE,{"derivedFrom":makeQuery(id+"F2.opExtrude","CAP_EDGE",EDGE,{"disambiguationData":[OSD([sQuery(id+"F0.wireOp",EDGE,"005f5cdd-0bdc-4fa0-b84f-56ab7e4a56270.MirrorCS")])],"isStart":true}),"instanceName":"1"});
            var Q40;
            Q40=makeQuery(id+"F3.opPattern","COPY",EDGE,{"derivedFrom":makeQuery(id+"F2.opExtrude","CAP_EDGE",EDGE,{"disambiguationData":[OSD([sQuery(id+"F0.wireOp",EDGE,"de5ad749-d6f0-4c98-9bd6-3e4d16faad500.MirrorCS")])],"isStart":true}),"instanceName":"1"});
            var Q41;
            Q41=makeQuery(id+"F3.opPattern","COPY",EDGE,{"derivedFrom":makeQuery(id+"F2.opExtrude","CAP_EDGE",EDGE,{"disambiguationData":[OSD([sQuery(id+"F0.wireOp",EDGE,"ogIBovJo-0tES-EHRu-C9qO-bWghCShUOrSJ")])],"isStart":true}),"instanceName":"1"});
            var Q42;
            Q42=makeQuery(id+"F3.opPattern","COPY",EDGE,{"derivedFrom":makeQuery(id+"F2.opExtrude","CAP_EDGE",EDGE,{"disambiguationData":[OSD([sQuery(id+"F0.wireOp",EDGE,"pasm8Eyo-fXrZ-fvG0-8Elu-paJzOGyL3H0m")])],"isStart":true}),"instanceName":"1"});
            var Q43;
            {var subQ0=sQuery(id+"F0.wireOp",EDGE,"E8");var subQ1=sQuery(id+"F0.wireOp",EDGE,"E1");var subQ2=makeQuery(id+"F0.imprint","INTERSECT",VERTEX,{"disambiguationData":[OD(0.0)],"derivedFrom":[subQ1,subQ0]});Q43=makeQuery(id+"F3.opPattern","COPY",EDGE,{"derivedFrom":makeQuery(id+"F2.opExtrude","CAP_EDGE",EDGE,{"disambiguationData":[OSD([subQ1]),TDD([makeQuery(id+"F0.imprint","IMPRINT",EDGE,{"disambiguationData":[TD([[makeQuery(id+"F0.imprint","INTERSECT",VERTEX,{"disambiguationData":[OD(0.0)],"derivedFrom":[sQuery(id+"F0.wireOp",EDGE,"E0.3"),subQ1]}),-1.0]])],"derivedFrom":subQ1}),makeQuery(id+"F0.imprint","IMPRINT",EDGE,{"disambiguationData":[TD([[subQ2,-1.0]])],"derivedFrom":subQ1})])],"isStart":true}),"instanceName":"1"});}
            var Q44;
            Q44=makeQuery(id+"F3.opPattern","COPY",EDGE,{"derivedFrom":makeQuery(id+"F2.opExtrude","CAP_EDGE",EDGE,{"disambiguationData":[OSD([sQuery(id+"F0.wireOp",EDGE,"E8")])],"isStart":true}),"instanceName":"1"});
            var Q45;
            {var subQ1=sQuery(id+"F0.wireOp",EDGE,"E8");var subQ2=sQuery(id+"F0.wireOp",EDGE,"E3");Q45=makeQuery(id+"F4.opBoolean","SPLIT",EDGE,{"disambiguationData":[TD([makeQuery(id+"F3.opPattern","COPY",FACE,{"derivedFrom":makeQuery(id+"F2.opExtrude","SWEPT_FACE",FACE,{"disambiguationData":[OSD([subQ1])]}),"instanceName":"1"})])],"derivedFrom":makeQuery(id+"F2.opExtrude","CAP_EDGE",EDGE,{"disambiguationData":[OSD([subQ2])],"isStart":true})});}
            var Q46;
            Q46=makeQuery(id+"F3.opPattern","COPY",EDGE,{"derivedFrom":makeQuery(id+"F2.opExtrude","CAP_EDGE",EDGE,{"disambiguationData":[OSD([sQuery(id+"F0.wireOp",EDGE,"E9")])],"isStart":true}),"instanceName":"2"});
            var Q47;
            {var subQ0=sQuery(id+"F0.wireOp",EDGE,"E1");var subQ1=sQuery(id+"F0.wireOp",EDGE,"E9");Q47=makeQuery(id+"F3.opPattern","COPY",EDGE,{"derivedFrom":makeQuery(id+"F2.opExtrude","CAP_EDGE",EDGE,{"disambiguationData":[OSD([subQ0]),TDD([makeQuery(id+"F0.imprint","IMPRINT",EDGE,{"disambiguationData":[TD([[makeQuery(id+"F0.imprint","INTERSECT",VERTEX,{"disambiguationData":[OD(0.0)],"derivedFrom":[subQ0,subQ1]}),-1.0]])],"derivedFrom":subQ0}),makeQuery(id+"F0.imprint","IMPRINT",EDGE,{"disambiguationData":[TD([[makeQuery(id+"F0.imprint","INTERSECT",VERTEX,{"disambiguationData":[OD(1.0)],"derivedFrom":[sQuery(id+"F0.wireOp",EDGE,"E0.3"),subQ0]}),1.0]])],"derivedFrom":subQ0})])],"isStart":true}),"instanceName":"2"});}
            var Q48;
            Q48=makeQuery(id+"F3.opPattern","COPY",EDGE,{"derivedFrom":makeQuery(id+"F2.opExtrude","CAP_EDGE",EDGE,{"disambiguationData":[OSD([sQuery(id+"F0.wireOp",EDGE,"005f5cdd-0bdc-4fa0-b84f-56ab7e4a56270.MirrorCS")])],"isStart":true}),"instanceName":"2"});
            var Q49;
            Q49=makeQuery(id+"F3.opPattern","COPY",EDGE,{"derivedFrom":makeQuery(id+"F2.opExtrude","CAP_EDGE",EDGE,{"disambiguationData":[OSD([sQuery(id+"F0.wireOp",EDGE,"de5ad749-d6f0-4c98-9bd6-3e4d16faad500.MirrorCS")])],"isStart":true}),"instanceName":"2"});
            var Q50;
            Q50=makeQuery(id+"F3.opPattern","COPY",EDGE,{"derivedFrom":makeQuery(id+"F2.opExtrude","CAP_EDGE",EDGE,{"disambiguationData":[OSD([sQuery(id+"F0.wireOp",EDGE,"ogIBovJo-0tES-EHRu-C9qO-bWghCShUOrSJ")])],"isStart":true}),"instanceName":"2"});
            var Q51;
            Q51=makeQuery(id+"F3.opPattern","COPY",EDGE,{"derivedFrom":makeQuery(id+"F2.opExtrude","CAP_EDGE",EDGE,{"disambiguationData":[OSD([sQuery(id+"F0.wireOp",EDGE,"pasm8Eyo-fXrZ-fvG0-8Elu-paJzOGyL3H0m")])],"isStart":true}),"instanceName":"2"});
            var Q52;
            {var subQ0=sQuery(id+"F0.wireOp",EDGE,"E8");var subQ1=sQuery(id+"F0.wireOp",EDGE,"E1");var subQ2=makeQuery(id+"F0.imprint","INTERSECT",VERTEX,{"disambiguationData":[OD(0.0)],"derivedFrom":[subQ1,subQ0]});Q52=makeQuery(id+"F3.opPattern","COPY",EDGE,{"derivedFrom":makeQuery(id+"F2.opExtrude","CAP_EDGE",EDGE,{"disambiguationData":[OSD([subQ1]),TDD([makeQuery(id+"F0.imprint","IMPRINT",EDGE,{"disambiguationData":[TD([[makeQuery(id+"F0.imprint","INTERSECT",VERTEX,{"disambiguationData":[OD(0.0)],"derivedFrom":[sQuery(id+"F0.wireOp",EDGE,"E0.3"),subQ1]}),-1.0]])],"derivedFrom":subQ1}),makeQuery(id+"F0.imprint","IMPRINT",EDGE,{"disambiguationData":[TD([[subQ2,-1.0]])],"derivedFrom":subQ1})])],"isStart":true}),"instanceName":"2"});}
            var Q53;
            Q53=makeQuery(id+"F3.opPattern","COPY",EDGE,{"derivedFrom":makeQuery(id+"F2.opExtrude","CAP_EDGE",EDGE,{"disambiguationData":[OSD([sQuery(id+"F0.wireOp",EDGE,"E8")])],"isStart":true}),"instanceName":"2"});
            fillet(context, id + "F12", {"entities" : qUnion([Q0, Q1, Q2, Q3, Q4, Q5, Q6, Q7, Q8, Q9, Q10, Q11, Q12, Q13, Q14, Q15, Q16, Q17, Q18, Q19, Q20, Q21, Q22, Q23, Q24, Q25, Q26, Q27, Q28, Q29, Q30, Q31, Q32, Q33, Q34, Q35, Q36, Q37, Q38, Q39, Q40, Q41, Q42, Q43, Q44, Q45, Q46, Q47, Q48, Q49, Q50, Q51, Q52, Q53]), "radius" : 3.5 * mm, "allowEdgeOverflow" : false});
        }
        {
            var Q0;
            {var subQ0=sQuery(id+"F0.wireOp",EDGE,"E1");var subQ1=sQuery(id+"F0.wireOp",EDGE,"E0.3");Q0=makeQuery(id+"F2.opExtrude","CAP_EDGE",EDGE,{"disambiguationData":[OSD([subQ0]),TDD([makeQuery(id+"F0.imprint","IMPRINT",EDGE,{"disambiguationData":[TD([[makeQuery(id+"F0.imprint","INTERSECT",VERTEX,{"disambiguationData":[OD(0.0)],"derivedFrom":[subQ1,subQ0]}),1.0]])],"derivedFrom":subQ0})])],"isStart":true});}
            var Q1;
            {var subQ0=sQuery(id+"F0.wireOp",EDGE,"E1");var subQ1=sQuery(id+"F0.wireOp",EDGE,"E0.3");Q1=makeQuery(id+"F3.opPattern","COPY",EDGE,{"derivedFrom":makeQuery(id+"F2.opExtrude","CAP_EDGE",EDGE,{"disambiguationData":[OSD([subQ0]),TDD([makeQuery(id+"F0.imprint","IMPRINT",EDGE,{"disambiguationData":[TD([[makeQuery(id+"F0.imprint","INTERSECT",VERTEX,{"disambiguationData":[OD(0.0)],"derivedFrom":[subQ1,subQ0]}),1.0]])],"derivedFrom":subQ0})])],"isStart":true}),"instanceName":"2"});}
            var Q2;
            {var subQ0=sQuery(id+"F0.wireOp",EDGE,"E1");var subQ1=sQuery(id+"F0.wireOp",EDGE,"E0.3");Q2=makeQuery(id+"F3.opPattern","COPY",EDGE,{"derivedFrom":makeQuery(id+"F2.opExtrude","CAP_EDGE",EDGE,{"disambiguationData":[OSD([subQ0]),TDD([makeQuery(id+"F0.imprint","IMPRINT",EDGE,{"disambiguationData":[TD([[makeQuery(id+"F0.imprint","INTERSECT",VERTEX,{"disambiguationData":[OD(0.0)],"derivedFrom":[subQ1,subQ0]}),1.0]])],"derivedFrom":subQ0})])],"isStart":true}),"instanceName":"1"});}
            var Q3;
            {var subQ0=sQuery(id+"F0.wireOp",EDGE,"E1");var subQ1=sQuery(id+"F0.wireOp",EDGE,"E0.3");Q3=makeQuery(id+"F3.opPattern","COPY",EDGE,{"derivedFrom":makeQuery(id+"F2.opExtrude","CAP_EDGE",EDGE,{"disambiguationData":[OSD([subQ0]),TDD([makeQuery(id+"F0.imprint","IMPRINT",EDGE,{"disambiguationData":[TD([[makeQuery(id+"F0.imprint","INTERSECT",VERTEX,{"disambiguationData":[OD(0.0)],"derivedFrom":[subQ1,subQ0]}),1.0]])],"derivedFrom":subQ0})])],"isStart":false}),"instanceName":"2"});}
            var Q4;
            {var subQ0=sQuery(id+"F0.wireOp",EDGE,"E1");var subQ1=sQuery(id+"F0.wireOp",EDGE,"E0.3");Q4=makeQuery(id+"F3.opPattern","COPY",EDGE,{"derivedFrom":makeQuery(id+"F2.opExtrude","CAP_EDGE",EDGE,{"disambiguationData":[OSD([subQ0]),TDD([makeQuery(id+"F0.imprint","IMPRINT",EDGE,{"disambiguationData":[TD([[makeQuery(id+"F0.imprint","INTERSECT",VERTEX,{"disambiguationData":[OD(0.0)],"derivedFrom":[subQ1,subQ0]}),1.0]])],"derivedFrom":subQ0})])],"isStart":false}),"instanceName":"1"});}
            var Q5;
            {var subQ0=sQuery(id+"F0.wireOp",EDGE,"E1");var subQ1=sQuery(id+"F0.wireOp",EDGE,"E0.3");Q5=makeQuery(id+"F2.opExtrude","CAP_EDGE",EDGE,{"disambiguationData":[OSD([subQ0]),TDD([makeQuery(id+"F0.imprint","IMPRINT",EDGE,{"disambiguationData":[TD([[makeQuery(id+"F0.imprint","INTERSECT",VERTEX,{"disambiguationData":[OD(0.0)],"derivedFrom":[subQ1,subQ0]}),1.0]])],"derivedFrom":subQ0})])],"isStart":false});}
            var Q6;
            {var subQ0=sQuery(id+"F0.wireOp",EDGE,"E1");var subQ1=sQuery(id+"F0.wireOp",EDGE,"E0.3");var subQ2=sQuery(id+"F0.wireOp",EDGE,"E8");Q6=makeQuery(id+"F12.opFillet","BLEND_EDGE",EDGE,{"blendedFrom":[makeQuery(id+"F3.opPattern","COPY",EDGE,{"derivedFrom":makeQuery(id+"F2.opExtrude","CAP_EDGE",EDGE,{"disambiguationData":[OSD([subQ2]),TDD([makeQuery(id+"F0.imprint","IMPRINT",EDGE,{"disambiguationData":[TD([[makeQuery(id+"F0.imprint","INTERSECT",VERTEX,{"disambiguationData":[OD(0.0)],"derivedFrom":[subQ0,subQ2]}),1.0]])],"derivedFrom":subQ2})])],"isStart":false}),"instanceName":"1"}),makeQuery(id+"F3.opPattern","COPY",FACE,{"derivedFrom":makeQuery(id+"F2.opExtrude","SWEPT_FACE",FACE,{"disambiguationData":[OSD([subQ0]),TDD([makeQuery(id+"F0.imprint","IMPRINT",EDGE,{"disambiguationData":[TD([[makeQuery(id+"F0.imprint","INTERSECT",VERTEX,{"disambiguationData":[OD(0.0)],"derivedFrom":[subQ1,subQ0]}),1.0]])],"derivedFrom":subQ0})])]}),"instanceName":"1"})],"blendedInto":[makeQuery(id+"F3.opPattern","COPY",FACE,{"derivedFrom":makeQuery(id+"F2.opExtrude","SWEPT_FACE",FACE,{"disambiguationData":[OSD([subQ0]),TDD([makeQuery(id+"F0.imprint","IMPRINT",EDGE,{"disambiguationData":[TD([[makeQuery(id+"F0.imprint","INTERSECT",VERTEX,{"disambiguationData":[OD(0.0)],"derivedFrom":[subQ1,subQ0]}),1.0]])],"derivedFrom":subQ0})])]}),"instanceName":"1"})]});}
            fillet(context, id + "F13", {"entities" : qUnion([Q0, Q1, Q2, Q3, Q4, Q5, Q6]), "radius" : 3.5 * mm, "tangentPropagation" : true, "allowEdgeOverflow" : false});
        }
        {
            var Q0;
            Q0=makeQuery(id+"F10.opPattern","COPY",FACE,{"derivedFrom":makeQuery(id+"F8.opExtrude","CAP_FACE",FACE,{"disambiguationData":[OSD([sQuery(id+"F1.wireOp",EDGE,"E19")])],"isStart":false}),"instanceName":"1"});
            var Q1;
            Q1=makeQuery(id+"F8.opExtrude","CAP_FACE",FACE,{"disambiguationData":[OSD([sQuery(id+"F1.wireOp",EDGE,"E16")])],"isStart":false});
            shell(context, id + "F14", {"entities" : qUnion([Q0, Q1]), "thickness" : 1.75 * mm});
        }
    });
